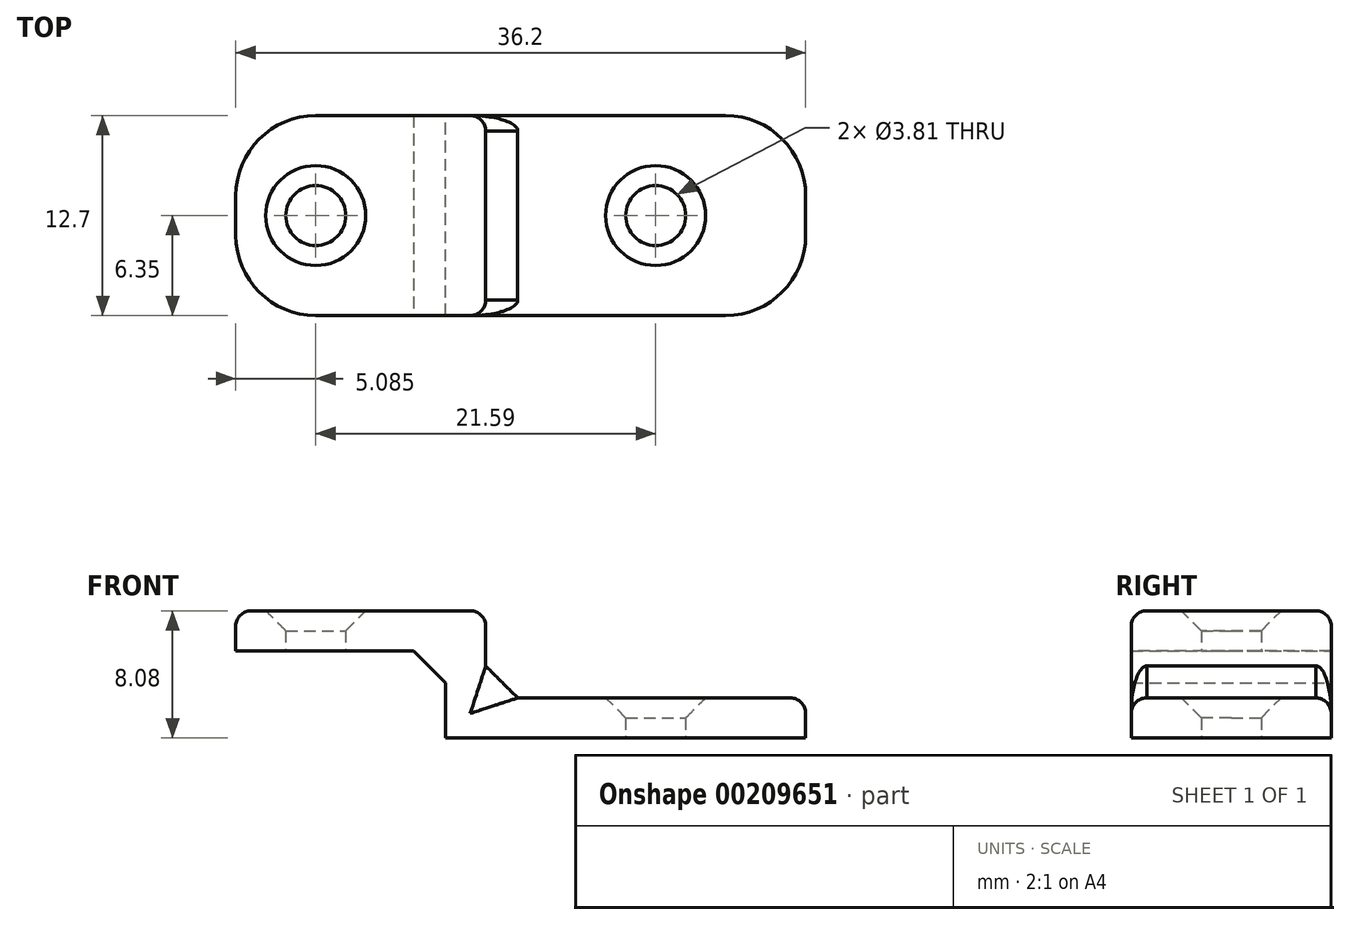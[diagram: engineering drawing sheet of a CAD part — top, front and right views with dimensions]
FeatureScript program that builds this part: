
annotation { "Feature Type Name" : "Feature", "Feature Type Description" : "" }
export const myFeature = defineFeature(function(context is Context, id is Id, definition is map)
    precondition{}
    {
        {
            var Q0;
            Q0=qCreatedBy(makeId("Front.planeOp"),FACE);
            var sketch = newSketch(context, id + "F0", { "sketchPlane" : qUnion([Q0])});
            skLineSegment(sketch, "E0", {"start": v(0, 0) * mm, "end": v(0, 1.5) * mm});
            skLineSegment(sketch, "E1", {"start": v(0, 1.5) * mm, "end": v(-13.33, 1.5) * mm});
            skLineSegment(sketch, "E2.0", {"start": v(2.54, 4.04) * mm, "end": v(-13.33, 4.04) * mm});
            skLineSegment(sketch, "E2.1", {"start": v(2.54, 0) * mm, "end": v(2.54, 4.04) * mm});
            skLineSegment(sketch, "E3", {"start": v(-13.33, 4.04) * mm, "end": v(-13.33, 1.5) * mm});
            skLineSegment(sketch, "E4", {"start": v(0, 3.3) * mm, "end": v(0, -26.78) * mm, "construction": true});
            skLineSegment(sketch, "E5", {"start": v(-31.43, 0) * mm, "end": v(38.23, 0) * mm, "construction": true});
            skLineSegment(sketch, "E6.MirrorCS", {"start": v(2.54, -4.04) * mm, "end": v(0, -4.04) * mm});
            skLineSegment(sketch, "E7.MirrorCS", {"start": v(0, 0) * mm, "end": v(0, -1.5) * mm});
            skLineSegment(sketch, "E8.MirrorCS", {"start": v(2.54, 0) * mm, "end": v(2.54, -1.5) * mm});
            skLineSegment(sketch, "E9.MirrorCS", {"start": v(22.86, -4.04) * mm, "end": v(22.86, -1.5) * mm});
            skLineSegment(sketch, "E10.MirrorCS", {"start": v(0, -4.04) * mm, "end": v(22.86, -4.04) * mm});
            skLineSegment(sketch, "E11.MirrorCS", {"start": v(2.54, -1.5) * mm, "end": v(22.86, -1.5) * mm});
            skLineSegment(sketch, "E12", {"start": v(0, -1.5) * mm, "end": v(0, -4.04) * mm});
            skSolve(sketch);
        }
        {
            var Q0;
            Q0=qSketchRegion(id+"F0",true);
            extrude(context, id + "F1", {"entities" : qUnion([Q0]), "depth" : 12.7 * mm});
        }
        {
            var Q0;
            Q0=qCreatedBy(makeId("Top.planeOp"),FACE);
            var sketch = newSketch(context, id + "F2", { "sketchPlane" : qUnion([Q0])});
            skLineSegment(sketch, "E13.0", {"start": v(-13.33, -12.7) * mm, "end": v(-13.33, 0) * mm, "construction": true});
            skCircle(sketch, "E14", {"center": v(-8.25, -6.35) * mm, "radius": 1.9 * mm});
            skPoint(sketch, "E14.centerSnap0", {"position": v(-13.33, -6.35) * mm});
            skLineSegment(sketch, "E15", {"start": v(0, -3.36) * mm, "end": v(0, 17.5) * mm, "construction": true});
            skLineSegment(sketch, "E16.0", {"start": v(2.54, -12.7) * mm, "end": v(2.54, 0) * mm, "construction": true});
            skCircle(sketch, "E17.MirrorC", {"center": v(13.33, -6.35) * mm, "radius": 1.9 * mm});
            skSolve(sketch);
        }
        {
            var Q0;
            Q0=qSketchRegion(id+"F2",true);
            extrude(context, id + "F3", {"entities" : qUnion([Q0]), "operationType" : NewBodyOperationType.REMOVE, "endBound" : BoundingType.THROUGH_ALL, "depth" : 25.4 * mm, "hasSecondDirection" : true, "secondDirectionBound" : SecondDirectionBoundingType.THROUGH_ALL, "secondDirectionOppositeDirection" : true, "secondDirectionDepth" : 25.4 * mm});
        }
        {
            var Q0;
            Q0=makeQuery(id+"F1.opExtrude","CAP_EDGE",EDGE,{"disambiguationData":[OSD([sQuery(id+"F0.wireOp",EDGE,"E3")])],"isStart":false});
            var Q1;
            Q1=makeQuery(id+"F1.opExtrude","CAP_EDGE",EDGE,{"disambiguationData":[OSD([sQuery(id+"F0.wireOp",EDGE,"E3")])],"isStart":true});
            var Q2;
            Q2=makeQuery(id+"F1.opExtrude","CAP_EDGE",EDGE,{"disambiguationData":[OSD([sQuery(id+"F0.wireOp",EDGE,"E9.MirrorCS")])],"isStart":false});
            var Q3;
            Q3=makeQuery(id+"F1.opExtrude","CAP_EDGE",EDGE,{"disambiguationData":[OSD([sQuery(id+"F0.wireOp",EDGE,"E9.MirrorCS")])],"isStart":true});
            fillet(context, id + "F4", {"entities" : qUnion([Q0, Q1, Q2, Q3]), "radius" : 5.08 * mm, "tangentPropagation" : true, "allowEdgeOverflow" : false});
        }
        {
            var Q0;
            Q0=makeQuery(id+"F1.opExtrude","CAP_EDGE",EDGE,{"disambiguationData":[OSD([sQuery(id+"F0.wireOp",EDGE,"E2.0")])],"isStart":false});
            var Q1;
            Q1=makeQuery(id+"F1.opExtrude","CAP_EDGE",EDGE,{"disambiguationData":[OSD([sQuery(id+"F0.wireOp",EDGE,"E2.1"),sQuery(id+"F0.wireOp",EDGE,"E8.MirrorCS")])],"isStart":false});
            var Q2;
            Q2=makeQuery(id+"F1.opExtrude","CAP_EDGE",EDGE,{"disambiguationData":[OSD([sQuery(id+"F0.wireOp",EDGE,"E2.1"),sQuery(id+"F0.wireOp",EDGE,"E8.MirrorCS")])],"isStart":true});
            var Q3;
            Q3=makeQuery(id+"F1.opExtrude","CAP_EDGE",EDGE,{"disambiguationData":[OSD([sQuery(id+"F0.wireOp",EDGE,"E11.MirrorCS")])],"isStart":false});
            var Q4;
            Q4=makeQuery(id+"F1.opExtrude","SWEPT_EDGE",EDGE,{"disambiguationData":[OSD([sQuery(id+"F0.wireOp",EDGE,"E2.0"),sQuery(id+"F0.wireOp",EDGE,"E2.1")])]});
            fillet(context, id + "F5", {"entities" : qUnion([Q0, Q1, Q2, Q3, Q4]), "radius" : 0.98 * mm, "tangentPropagation" : true, "allowEdgeOverflow" : false});
        }
        {
            var Q0;
            Q0=makeQuery(id+"F3.boolean.opBoolean","INTERSECT",EDGE,{"derivedFrom":[makeQuery(id+"F1.opExtrude","SWEPT_FACE",FACE,{"disambiguationData":[OSD([sQuery(id+"F0.wireOp",EDGE,"E2.0")])]}),makeQuery(id+"F3.opExtrude","SWEPT_FACE",FACE,{"disambiguationData":[OSD([sQuery(id+"F2.wireOp",EDGE,"E14")])]})]});
            var Q1;
            Q1=makeQuery(id+"F3.boolean.opBoolean","INTERSECT",EDGE,{"derivedFrom":[makeQuery(id+"F1.opExtrude","SWEPT_FACE",FACE,{"disambiguationData":[OSD([sQuery(id+"F0.wireOp",EDGE,"E11.MirrorCS")])]}),makeQuery(id+"F3.opExtrude","SWEPT_FACE",FACE,{"disambiguationData":[OSD([sQuery(id+"F2.wireOp",EDGE,"E17.MirrorC")])]})]});
            chamfer(context, id + "F6", {"entities" : qUnion([Q0, Q1]), "width" : 1.27 * mm, "tangentPropagation" : true});
        }
        {
            var Q0;
            Q0=makeQuery(id+"F1.opExtrude","SWEPT_EDGE",EDGE,{"disambiguationData":[OSD([sQuery(id+"F0.wireOp",EDGE,"E8.MirrorCS"),sQuery(id+"F0.wireOp",EDGE,"E11.MirrorCS")])]});
            var Q1;
            Q1=makeQuery(id+"F1.opExtrude","SWEPT_EDGE",EDGE,{"disambiguationData":[OSD([sQuery(id+"F0.wireOp",EDGE,"E0"),sQuery(id+"F0.wireOp",EDGE,"E1")])]});
            chamfer(context, id + "F7", {"entities" : qUnion([Q0, Q1]), "width" : 2.03 * mm, "tangentPropagation" : true});
        }
    });
